# Revit family: Basin-Ligature_Resistant-Whitehall-BestCare-WH3743
name_source: partatom
category: Plumbing Fixtures
units: mm (PartAtom-declared; Revit-internal decimal feet)

## family parameters
Cut with Voids When Loaded = No
Host = Face
OmniClass Number = 23.45.05.14.14
OmniClass Title = Sinks/Lavatories
Part Type = Normal
Room Calculation Point = No
Round Connector Dimension = Use Diameter
Shared = Yes

## types (1)
- WH3743
    -LCC High Pressure Laminate Optional Color Veranda Teak is Standard = No
    -MC Mounting Carrier (Bariatric) = No
    -OCC Optional Corterra Color - Specify ___________ = No
    -WHST70-12 Tempering Valve With Integral Mounting Feet Brass Body With 1/2” NPT Connections = No
    ADA Compliant = Yes
    Assembly Code = D2010310
    Bariatric Enclosure Material = Stainless Steel-Whitehall-Laminate Veranda Teak
    Bowl Shape = D-Shape Bowl
    CW Connection = Yes
    CWFU = 2
    Cold Water Connection Diameter = 1/2"
    Countertop and Basin Material = Corterra-Whitehall-Blanco Gloss OCC11 (White)
    Default Elevation = 34"
    Description = Whitehall Ligature Resistant ADA Compliant Bariatric Corterra® Basin
    HW Connection = Yes
    HWFU = 2
    Height = 38"
    Hot Water Connection Diameter = 1/2"
    IAPMO Compliance = Each standard height Washbasin complies
with ANSI, UFAS, and ADA requirements.
    Length = 31"
    Manufacturer = Whitehall Mfg
    Material = Corterra-Whitehall-Blanco Gloss OCC11 (White)
    Model = WH3743
    Operating Pressure = 30 to 100 PSI
    URL = http://www.whitehallmfg.com
    Vent Connection = No
    WFU = 3
    WH3375-SO Optional Ligature Resistant Faucet = Yes
    Waste Connection = Yes
    Waste Connection Diameter = 1 1/2"
    Waste Connection Radius = 3/4"
    Width = 22"

## geometry (parser evidence)
native form markers: Sweep x5
no freeform markers — native parametric forms only
